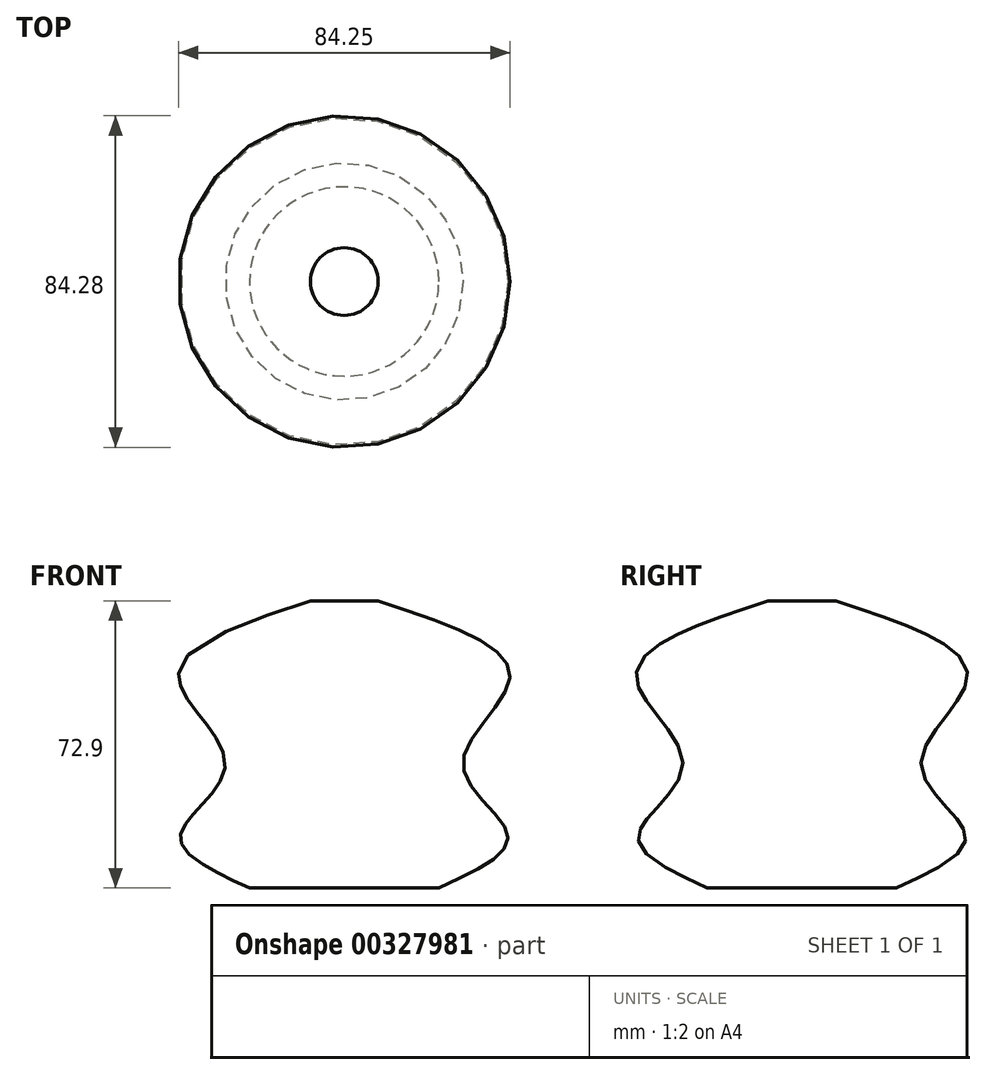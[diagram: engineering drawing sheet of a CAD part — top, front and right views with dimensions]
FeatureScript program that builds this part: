
annotation { "Feature Type Name" : "Feature", "Feature Type Description" : "" }
export const myFeature = defineFeature(function(context is Context, id is Id, definition is map)
    precondition{}
    {
        {
            var Q0;
            Q0=qCreatedBy(makeId("Front.planeOp"),FACE);
            var sketch = newSketch(context, id + "F0", { "sketchPlane" : qUnion([Q0])});
            skLineSegment(sketch, "E0", {"start": v(0, 35.14) * mm, "end": v(0, -37.76) * mm});
            skLineSegment(sketch, "E1", {"start": v(0, -37.76) * mm, "end": v(24.06, -37.76) * mm});
            skLineSegment(sketch, "E2", {"start": v(0, 35.14) * mm, "end": v(8.6, 35.14) * mm});
            skFitSpline(sketch, "E3", {"points": [v(24.06, -37.76) * mm, v(41.56, -24.35) * mm, v(30.18, -6.56) * mm, v(42.14, 15.9) * mm, v(8.6, 35.14) * mm], "startDerivative": vector(120.18, 54.34) * mm, "endDerivative": vector(-168.55, 54.85) * mm});
            skSolve(sketch);
        }
        {
            var Q0;
            Q0=makeQuery(id+"F0.imprint","IMPRINT",FACE,{"disambiguationData":[TD([[makeQuery(id+"F0.imprint","IMPRINT",EDGE,{"derivedFrom":sQuery(id+"F0.wireOp",EDGE,"E0")}),1.0]])]});
            var Q1;
            Q1=sQuery(id+"F0.wireOp",EDGE,"E0");
            revolve(context, id + "F1", {"surfaceOperationType" : NewSurfaceOperationType.NEW, "entities" : qUnion([Q0]), "axis" : qUnion([Q1]), "revolveType" : RevolveType.FULL});
        }
    });
